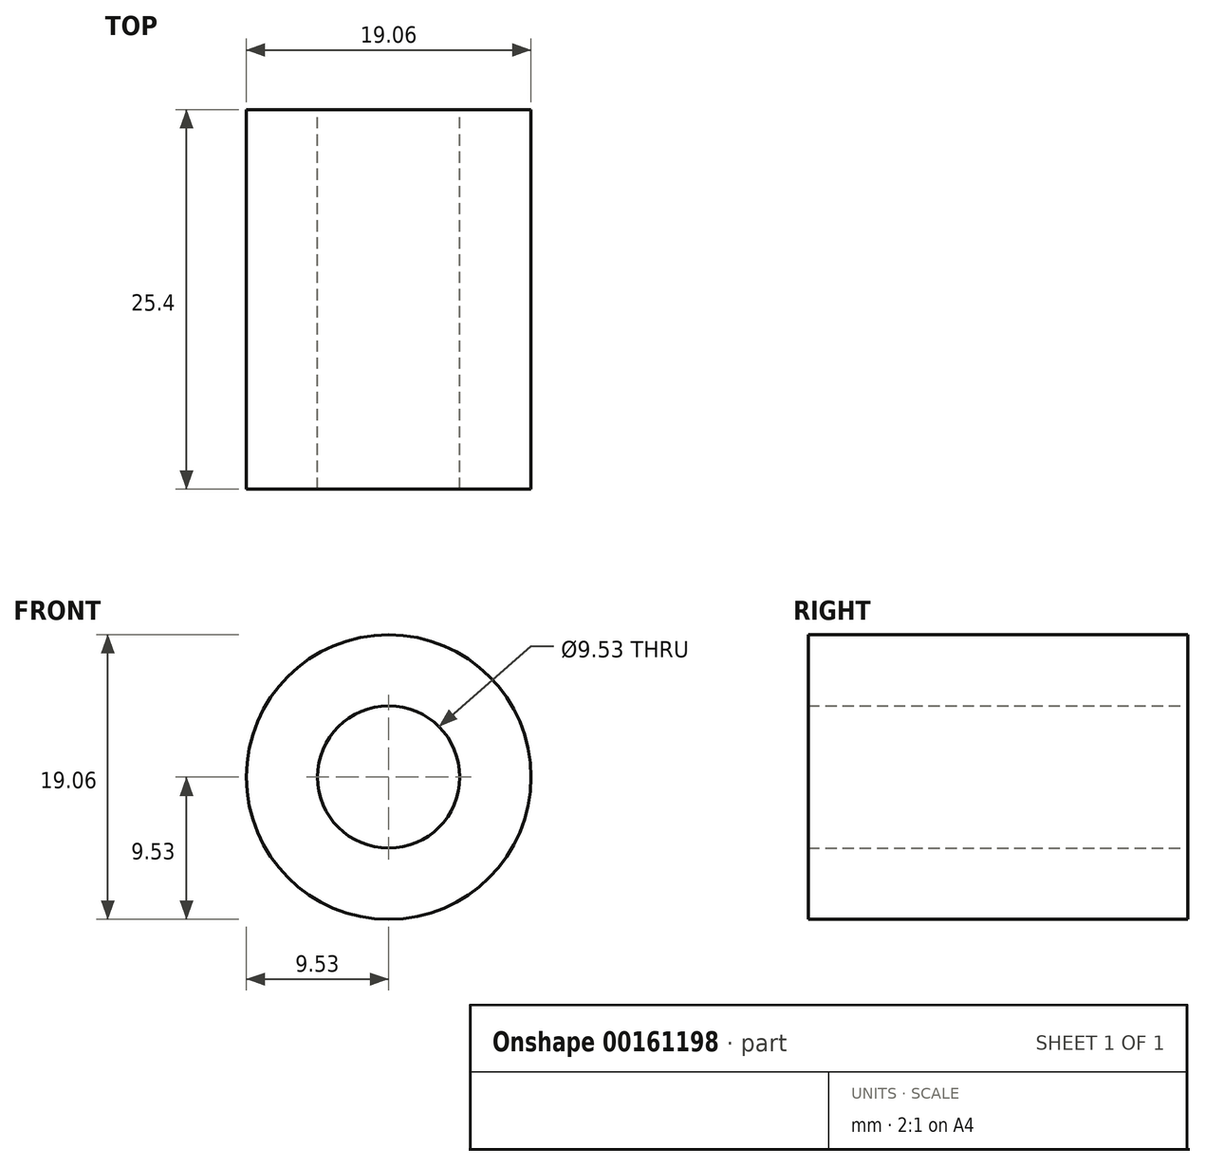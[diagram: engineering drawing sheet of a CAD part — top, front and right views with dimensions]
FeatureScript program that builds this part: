
annotation { "Feature Type Name" : "Feature", "Feature Type Description" : "" }
export const myFeature = defineFeature(function(context is Context, id is Id, definition is map)
    precondition{}
    {
        {
            var Q0;
            Q0=qCreatedBy(makeId("Front.planeOp"),FACE);
            var sketch = newSketch(context, id + "F0", { "sketchPlane" : qUnion([Q0])});
            skCircle(sketch, "E0", {"center": v(0, 0) * mm, "radius": 9.53 * mm});
            skSolve(sketch);
        }
        {
            var Q0;
            Q0 = qSketchRegion(id + "F0", true);
            extrude(context, id + "F1", {"entities" : qUnion([Q0]), "depth" : 25.4 * mm});
        }
        {
            var Q0;
            Q0=qCreatedBy(makeId("Front.planeOp"),FACE);
            var sketch = newSketch(context, id + "F2", { "sketchPlane" : qUnion([Q0])});
            skLineSegment(sketch, "E1.bottom", {"start": v(4.76, -4.76) * mm, "end": v(-4.76, -4.76) * mm});
            skLineSegment(sketch, "E1.top", {"start": v(4.76, 4.76) * mm, "end": v(-4.76, 4.76) * mm});
            skLineSegment(sketch, "E1.left", {"start": v(4.76, -4.76) * mm, "end": v(4.76, 4.76) * mm});
            skLineSegment(sketch, "E1.right", {"start": v(-4.76, -4.76) * mm, "end": v(-4.76, 4.76) * mm});
            skPoint(sketch, "E1.middle", {"position": v(0, 0) * mm});
            skCircle(sketch, "E2", {"center": v(0, 0) * mm, "radius": 4.76 * mm});
            skSolve(sketch);
        }
        {
            var Q0;
            {var subQ0=sQuery(id+"F2.wireOp",EDGE,"E2");var subQ1=makeQuery(id+"F2.imprint","INTERSECT",VERTEX,{"derivedFrom":[sQuery(id+"F2.wireOp",EDGE,"E1.top"),subQ0]});Q0=makeQuery(id+"F2.imprint","IMPRINT",FACE,{"disambiguationData":[TD([[makeQuery(id+"F2.imprint","IMPRINT",EDGE,{"disambiguationData":[TD([[subQ1,1.0]])],"derivedFrom":subQ0}),1.0]])]});}
            extrude(context, id + "F3", {"entities" : qUnion([Q0]), "operationType" : NewBodyOperationType.REMOVE, "depth" : 30.6 * mm});
        }
    });
